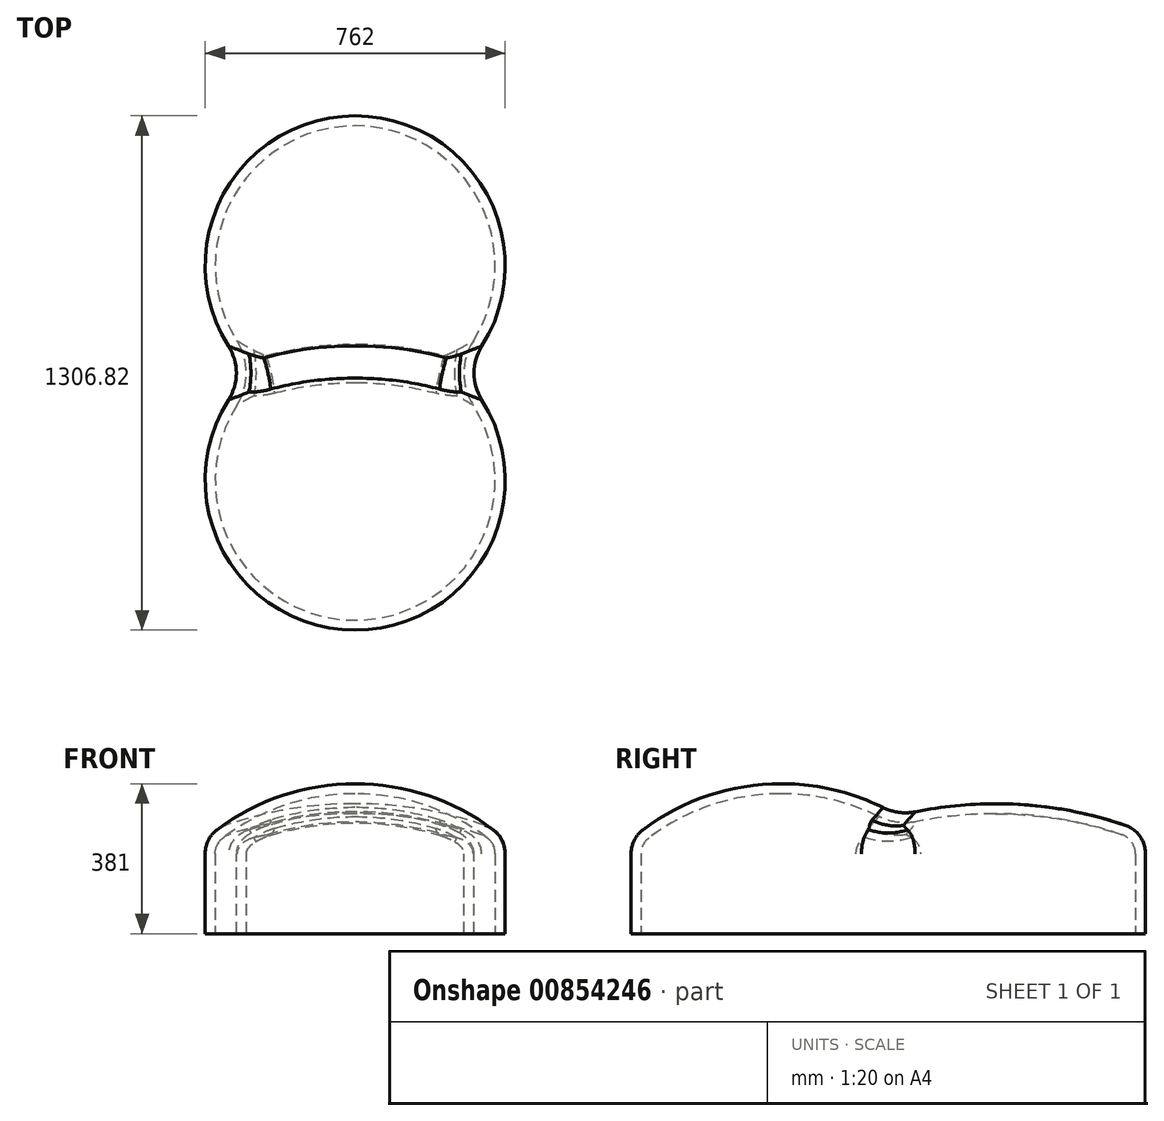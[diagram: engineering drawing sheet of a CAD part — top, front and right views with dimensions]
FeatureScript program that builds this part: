
annotation { "Feature Type Name" : "Feature", "Feature Type Description" : "" }
export const myFeature = defineFeature(function(context is Context, id is Id, definition is map)
    precondition{}
    {
        {
            var Q0;
            Q0=qCreatedBy(makeId("Top.planeOp"),FACE);
            var sketch = newSketch(context, id + "F0", { "sketchPlane" : qUnion([Q0])});
            skArc(sketch, "E0", {"start": v(228.58, 0) * mm, "mid": v(0, 628) * mm, "end": v(-228.58, 0) * mm});
            skArc(sketch, "E1", {"start": v(-228.58, 0) * mm, "mid": v(0, -628) * mm, "end": v(228.58, 0) * mm});
            skLineSegment(sketch, "E2", {"start": v(0, 272.4) * mm, "end": v(0, -272.4) * mm, "construction": true});
            skLineSegment(sketch, "E3", {"start": v(-228.58, 0) * mm, "end": v(0, 272.4) * mm, "construction": true});
            skLineSegment(sketch, "E4", {"start": v(228.58, 0) * mm, "end": v(0, 272.4) * mm, "construction": true});
            skSolve(sketch);
        }
        {
            var Q0;
            Q0 = qSketchRegion(id + "F0", true);
            extrude(context, id + "F1", {"entities" : qUnion([Q0]), "depth" : 203.2 * mm, "offsetDistance" : 25.4 * mm});
        }
        {
            var Q0;
            Q0=qCreatedBy(makeId("Front.planeOp"),FACE);
            var sketch = newSketch(context, id + "F2", { "sketchPlane" : qUnion([Q0])});
            skLineSegment(sketch, "E5", {"start": v(-355.6, 203.2) * mm, "end": v(0, 330.2) * mm});
            skLineSegment(sketch, "E6", {"start": v(0, 330.2) * mm, "end": v(355.6, 203.2) * mm});
            skLineSegment(sketch, "E7", {"start": v(355.6, 203.2) * mm, "end": v(-355.6, 203.2) * mm});
            skLineSegment(sketch, "E8", {"start": v(0, 203.2) * mm, "end": v(0, 0) * mm, "construction": true});
            skSolve(sketch);
        }
        {
            var Q0;
            Q0=qCreatedBy(makeId("Right.planeOp"),FACE);
            var sketch = newSketch(context, id + "F3", { "sketchPlane" : qUnion([Q0])});
            skLineSegment(sketch, "E9", {"start": v(634.83, 330.65) * mm, "end": v(401.9, 330.65) * mm});
            skLineSegment(sketch, "E10", {"start": v(401.9, 330.65) * mm, "end": v(634.83, 202.19) * mm});
            skLineSegment(sketch, "E11", {"start": v(634.83, 202.19) * mm, "end": v(634.83, 330.65) * mm});
            skLineSegment(sketch, "E12", {"start": v(-636.35, 330.65) * mm, "end": v(-434.4, 330.65) * mm});
            skLineSegment(sketch, "E13", {"start": v(-434.4, 330.65) * mm, "end": v(-639.09, 202.19) * mm});
            skLineSegment(sketch, "E14", {"start": v(-639.09, 202.19) * mm, "end": v(-636.35, 330.65) * mm});
            skSolve(sketch);
        }
        {
            var Q0;
            Q0=qCreatedBy(makeId("Right.planeOp"),FACE);
            var sketch = newSketch(context, id + "F4", { "sketchPlane" : qUnion([Q0])});
            skLineSegment(sketch, "E15", {"start": v(-272.4, 203.2) * mm, "end": v(-272.4, 355.6) * mm});
            skLineSegment(sketch, "E16", {"start": v(-272.4, 203.2) * mm, "end": v(-628, 203.2) * mm});
            skLineSegment(sketch, "E17", {"start": v(-272.4, 203.2) * mm, "end": v(-272.4, -196.85) * mm, "construction": true});
            skLineSegment(sketch, "E18", {"start": v(-272.4, 355.6) * mm, "end": v(-628, 203.2) * mm, "construction": true});
            skArc(sketch, "E19", {"start": v(-272.4, 355.6) * mm, "mid": v(-449.11, 326.92) * mm, "end": v(-607.69, 243.84) * mm});
            skArc(sketch, "E20", {"start": v(-607.69, 243.84) * mm, "mid": v(-622.64, 225.92) * mm, "end": v(-628, 203.2) * mm});
            skLineSegment(sketch, "E21", {"start": v(-272.4, 355.6) * mm, "end": v(-46.65, 355.6) * mm, "construction": true});
            skSolve(sketch);
        }
        {
            var Q0;
            Q0=makeQuery(id+"F4.imprint","IMPRINT",FACE,{"disambiguationData":[TD([[makeQuery(id+"F4.imprint","IMPRINT",EDGE,{"derivedFrom":sQuery(id+"F4.wireOp",EDGE,"E15")}),1.0]])]});
            var Q1;
            Q1=sQuery(id+"F4.wireOp",EDGE,"E17");
            revolve(context, id + "F5", {"operationType" : NewBodyOperationType.ADD, "surfaceOperationType" : NewSurfaceOperationType.NEW, "entities" : qUnion([Q0]), "axis" : qUnion([Q1]), "revolveType" : RevolveType.FULL});
        }
        {
            var Q0;
            Q0=qCreatedBy(makeId("Right.planeOp"),FACE);
            var sketch = newSketch(context, id + "F6", { "sketchPlane" : qUnion([Q0])});
            skLineSegment(sketch, "E22", {"start": v(272.4, 203.2) * mm, "end": v(628, 203.2) * mm});
            skArc(sketch, "E23", {"start": v(628, 203.2) * mm, "mid": v(618.54, 232.73) * mm, "end": v(593.68, 251.25) * mm});
            skLineSegment(sketch, "E24", {"start": v(272.4, 203.2) * mm, "end": v(272.4, 304.8) * mm});
            skArc(sketch, "E25", {"start": v(593.68, 251.25) * mm, "mid": v(435.26, 291.32) * mm, "end": v(272.4, 304.8) * mm});
            skLineSegment(sketch, "E26", {"start": v(272.4, 304.8) * mm, "end": v(272.4, 354.8) * mm, "construction": true});
            skSolve(sketch);
        }
        {
            var Q0;
            Q0 = qSketchRegion(id + "F6", true);
            var Q1;
            Q1=sQuery(id+"F6.wireOp",EDGE,"E26");
            revolve(context, id + "F7", {"operationType" : NewBodyOperationType.ADD, "surfaceOperationType" : NewSurfaceOperationType.NEW, "entities" : qUnion([Q0]), "axis" : qUnion([Q1]), "revolveType" : RevolveType.FULL});
        }
        {
            var Q0;
            {var subQ0=sQuery(id+"F0.wireOp",EDGE,"E1");var subQ1=sQuery(id+"F0.wireOp",EDGE,"E0");Q0=makeQuery(id+"F1.opExtrude","SWEPT_EDGE",EDGE,{"disambiguationData":[OSD([subQ1,subQ0]),TDD([makeQuery(id+"F0.imprint","INTERSECT",VERTEX,{"disambiguationData":[OD(1.0)],"derivedFrom":[subQ1,subQ0]})])]});}
            fillet(context, id + "F8", {"entities" : qUnion([Q0]), "radius" : 152.4 * mm, "tangentPropagation" : true, "allowEdgeOverflow" : false});
        }
        {
            var Q0;
            Q0=makeQuery(id+"F1.opExtrude","CAP_FACE",FACE,{"disambiguationData":[OSD([sQuery(id+"F0.wireOp",EDGE,"E0"),sQuery(id+"F0.wireOp",EDGE,"E1")])],"isStart":true});
            shell(context, id + "F9", {"entities" : qUnion([Q0]), "thickness" : 25.4 * mm, "oppositeDirection" : true});
        }
    });
